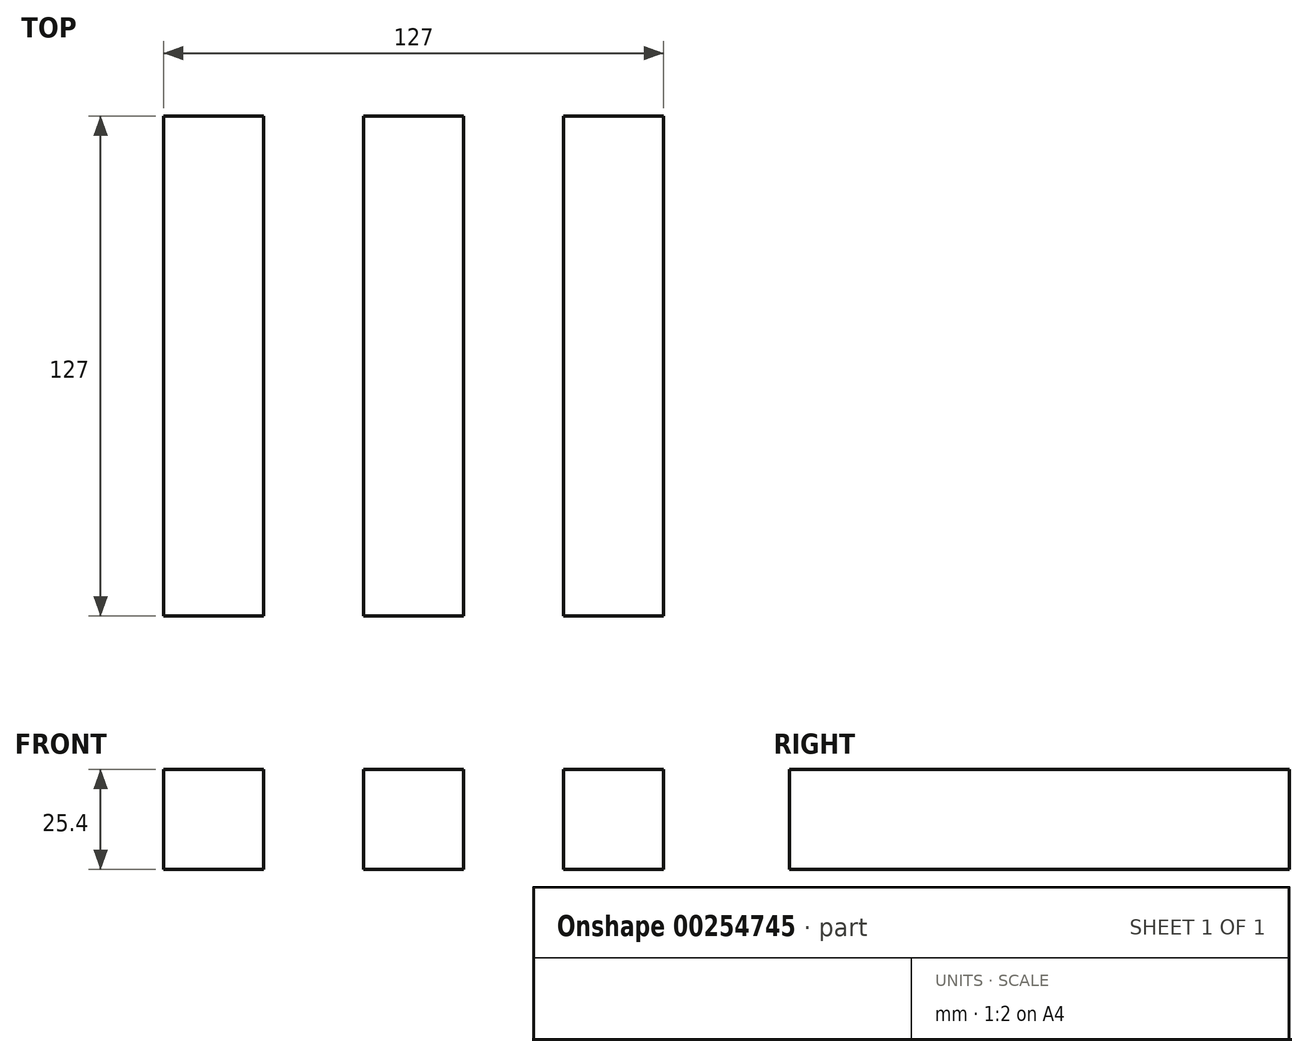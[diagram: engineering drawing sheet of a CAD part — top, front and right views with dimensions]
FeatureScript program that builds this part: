
annotation { "Feature Type Name" : "Feature", "Feature Type Description" : "" }
export const myFeature = defineFeature(function(context is Context, id is Id, definition is map)
    precondition{}
    {
        {
            var Q0;
            Q0=qCreatedBy(makeId("Front.planeOp"),FACE);
            var sketch = newSketch(context, id + "F0", { "sketchPlane" : qUnion([Q0])});
            skLineSegment(sketch, "E0.bottom", {"start": v(-38.1, 12.7) * mm, "end": v(-63.5, 12.7) * mm});
            skLineSegment(sketch, "E0.top", {"start": v(-38.1, -12.7) * mm, "end": v(-63.5, -12.7) * mm});
            skLineSegment(sketch, "E0.left", {"start": v(-38.1, 12.7) * mm, "end": v(-38.1, -12.7) * mm});
            skLineSegment(sketch, "E0.right", {"start": v(-63.5, 12.7) * mm, "end": v(-63.5, -12.7) * mm});
            skPoint(sketch, "E0.middle", {"position": v(-50.8, 0) * mm});
            skLineSegment(sketch, "E1.bottom", {"start": v(-12.7, 12.7) * mm, "end": v(12.7, 12.7) * mm});
            skLineSegment(sketch, "E1.top", {"start": v(-12.7, -12.7) * mm, "end": v(12.7, -12.7) * mm});
            skLineSegment(sketch, "E1.left", {"start": v(-12.7, 12.7) * mm, "end": v(-12.7, -12.7) * mm});
            skLineSegment(sketch, "E1.right", {"start": v(12.7, 12.7) * mm, "end": v(12.7, -12.7) * mm});
            skPoint(sketch, "E1.middle", {"position": v(0, 0) * mm});
            skLineSegment(sketch, "E2.bottom", {"start": v(63.5, 12.7) * mm, "end": v(38.1, 12.7) * mm});
            skLineSegment(sketch, "E2.top", {"start": v(63.5, -12.7) * mm, "end": v(38.1, -12.7) * mm});
            skLineSegment(sketch, "E2.left", {"start": v(63.5, 12.7) * mm, "end": v(63.5, -12.7) * mm});
            skLineSegment(sketch, "E2.right", {"start": v(38.1, 12.7) * mm, "end": v(38.1, -12.7) * mm});
            skPoint(sketch, "E2.middle", {"position": v(50.8, 0) * mm});
            skSolve(sketch);
        }
        {
            var Q0;
            Q0 = qSketchRegion(id + "F0", true);
            extrude(context, id + "F1", {"entities" : qUnion([Q0]), "endBound" : BoundingType.SYMMETRIC, "depth" : 127 * mm});
        }
    });
